# Revit family: equip-sink-clsrm-elkay-s-celebrity-cdkrad2517-vrc
name_source: partatom
category: Plumbing Fixtures
units: mm (PartAtom-declared; Revit-internal decimal feet)

## family parameters
Always vertical = Yes
Cut with Voids When Loaded = No
OmniClass Number = 23.45.05.14.14.27
OmniClass Title = Service Sinks
Part Type = Normal
Room Calculation Point = No
Round Connector Dimension = Use Radius
Shared = No
Work Plane-Based = Yes

## types (2) — shared parameters
Assembly Code = D2010410
Back Faucet CL to Back = 0' - 2 1/4"
Back Faucet Hole One to CL = 0' - 4"
Back Faucet Hole OneTwo = No
Back Faucet Hole OneTwo Top = 0' - 0 1/8"
Back Faucet Hole Three = No
Back Faucet Hole Three Top = 0' - 0 1/8"
Bowl Drain Location FB = 0' - 7"
Bowl Length = 1' - 3 3/4"
Bowl Width = 1' - 2"
Bubbler Back Left = Yes
Bubbler Back Left Top = 0' - 0 1/2"
Bubbler Back Right = No
Bubbler Back Right Top = 0' - 0 1/8"
Bubbler CW Flow Rate = 2 GPM
Bubbler Front Left = No
Bubbler Front Left Radius = 0' - 0 9/16"
Bubbler Front Left Top = 0' - 0 1/8"
Bubbler Front Right = Yes
Bubbler Front Right Radius = 0' - 0 9/16"
Bubbler Front Right Top = 0' - 0 1/2"
Bubbler Left From Edge = 0' - 2 1/4"
Bubbler Material = Metal - Steel - Stainless - Chrome
Bubbler Nominal Dia = 0' - 0 1/2"
Bubbler Nominal Radius = 0' - 0 1/4"
Bubbler Part = LKVR1141A
Bubbler Right from Edge = 0' - 2 1/4"
CW Flow Rate = 2 GPM
Default Elevation = 3' - 0"
Description = Lustertone Classroom Single Bowl Sink
Drain CL LR to Left Bowl Edge = 0' - 7 7/8"
Drain Material = Metal - Steel - Stainless - Chrome
Drain Part = LKVR18
Faucet Material = Metal - Steel - Stainless - Chrome
Faucet Part = LKDVR208513-L
HW Flow Rate = 2 GPM
Left Faucet Hole OneTwo = No
Left Faucet Hole OneTwo Top = 0' - 0 1/8"
Left Faucet Hole Three = No
Left Faucet Hole Three Top = 0' - 0 1/8"
Manufacturer = Elkay Manufacturing
MasterFormat Number = 22.42.16.16
MasterFormat Title = Commercial Sinks
Minimum Cabinet Width = 30"
Nominal Dia = 0' - 0 3/8"
Nominal Radius = 0' - 0 3/16"
OmniClass Code = 23.45.05.14.14.27
OmniClass Title = Service Sinks
Right Faucet Hole One to CL = 0' - 4"
Right Faucet Hole OneTwo = No
Right Faucet Hole OneTwo Top = 0' - 0 1/8"
Right Faucet Hole Three = No
Right Faucet Hole Three Top = 0' - 0 1/8"
Sanitary Flow Rate = 10 GPM
Sanitary Nominal Dia = 0' - 1 1/2"
Sanitary Nominal Radius = 0' - 0 3/4"
Sink Ledge Back Width = 0' - 1 1/2"
Sink Ledge Back Width Hidden = 0' - 1 1/2"
Sink Ledge Front Width = 0' - 1 1/2"
Sink Ledge Front Width Hidden = 0' - 1 1/2"
Sink Ledge Left Width = 0' - 4 5/8"
Sink Ledge Left Width Hidden = 0' - 4 5/8"
Sink Ledge Right Width = 0' - 4 5/8"
Sink Ledge Right Width Hidden = 0' - 4 5/8"
Sink Length = 2' - 1"
Sink Material = Metal - Steel - Stainless - Chrome
Sink Width = 1' - 5"
Specification Sheet URL = http://www.elkayusa.com
Stem Material = Metal - Steel
URL = www.elkayusa.com

## per-type parameters (varying)
| type | Bowl Depth | Sink Part |
| CDKR2517VRC | 0' - 6 7/8" | CDKR2517-2 |
| CDKAD2517VRC | 0' - 6 1/2" | CDKAD2517-2 |

note: column(s) folded — value = type name in every type: Model

## geometry (parser evidence)
native form markers: Sweep x13
no freeform markers — native parametric forms only
